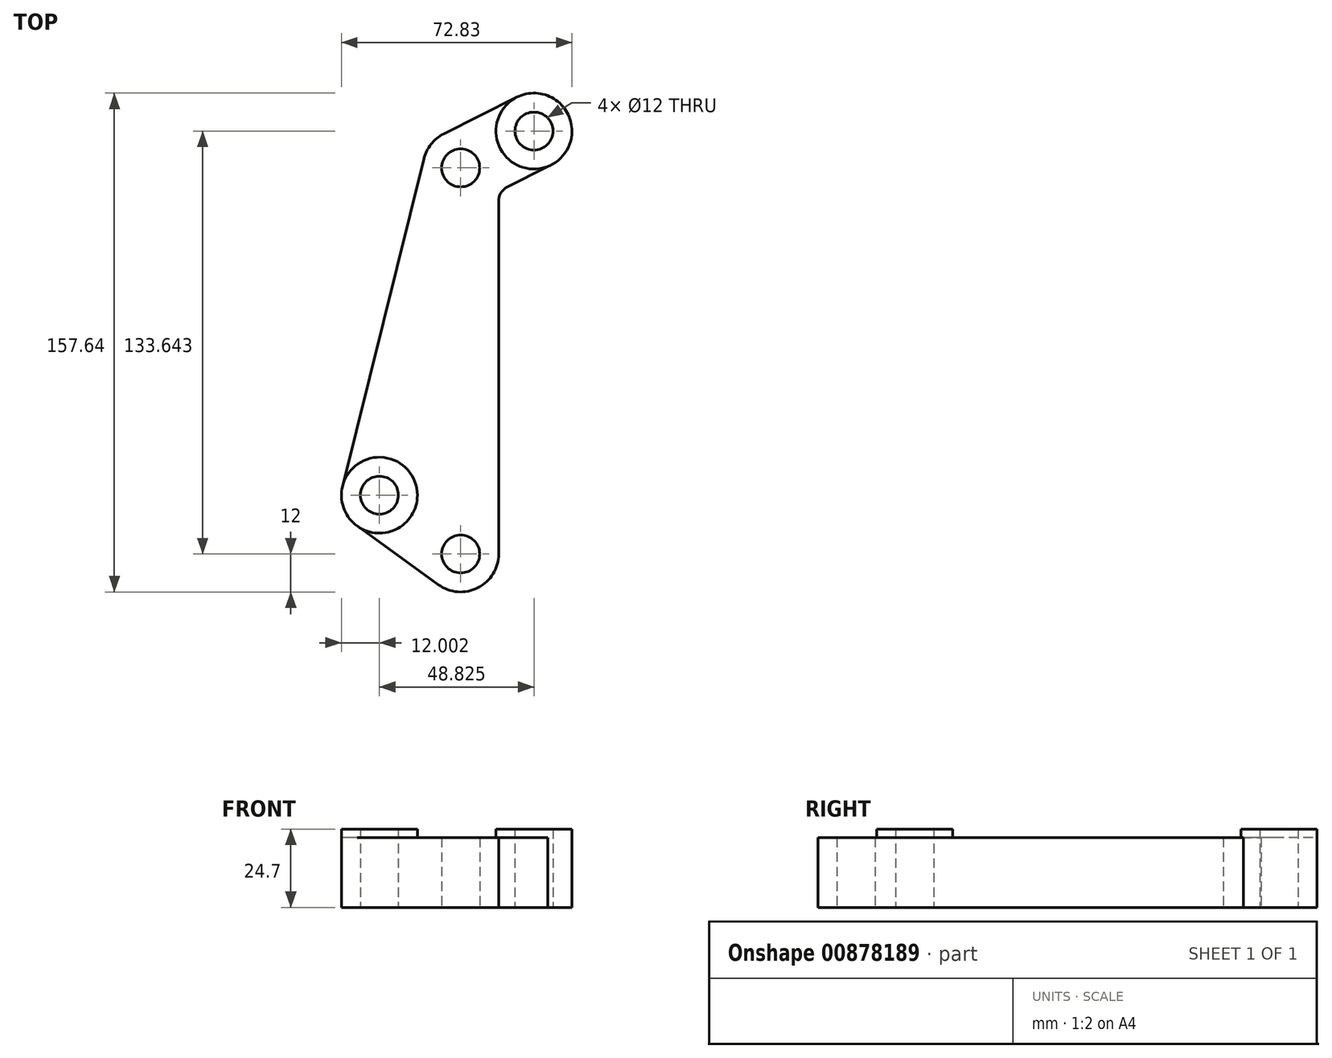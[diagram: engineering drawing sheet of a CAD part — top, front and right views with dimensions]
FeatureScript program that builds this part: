
annotation { "Feature Type Name" : "Feature", "Feature Type Description" : "" }
export const myFeature = defineFeature(function(context is Context, id is Id, definition is map)
    precondition{}
    {
        {
            var Q0;
            Q0=qCreatedBy(makeId("Top.planeOp"),FACE);
            var sketch = newSketch(context, id + "F0", { "sketchPlane" : qUnion([Q0])});
            skCircle(sketch, "E0", {"center": v(0, 0) * mm, "radius": 73.5 * mm, "construction": true});
            skCircle(sketch, "E1", {"center": v(0, 0) * mm, "radius": 70 * mm, "construction": true});
            skCircle(sketch, "E2", {"center": v(-34.34, 61) * mm, "radius": 6 * mm});
            skCircle(sketch, "E3", {"center": v(-34.34, -61) * mm, "radius": 6 * mm});
            skCircle(sketch, "E4", {"center": v(-60.02, -42.43) * mm, "radius": 6 * mm});
            skCircle(sketch, "E5", {"center": v(-11.2, 72.64) * mm, "radius": 6 * mm});
            skLineSegment(sketch, "E6", {"start": v(-11.2, 72.64) * mm, "end": v(-60.02, -42.43) * mm, "construction": true});
            skLineSegment(sketch, "E7", {"start": v(-34.34, 61) * mm, "end": v(-34.34, -61) * mm, "construction": true});
            skCircle(sketch, "E8", {"center": v(-60.02, -42.43) * mm, "radius": 12 * mm});
            skCircle(sketch, "E9", {"center": v(-34.34, -61) * mm, "radius": 12 * mm});
            skCircle(sketch, "E10", {"center": v(-11.2, 72.64) * mm, "radius": 12 * mm});
            skCircle(sketch, "E11", {"center": v(-34.34, 61) * mm, "radius": 12 * mm});
            skLineSegment(sketch, "E12", {"start": v(-34.34, -61) * mm, "end": v(-22.34, -61) * mm});
            skLineSegment(sketch, "E13", {"start": v(-16.59, 83.36) * mm, "end": v(-39.73, 71.72) * mm});
            skLineSegment(sketch, "E14", {"start": v(-45.98, 63.9) * mm, "end": v(-71.66, -39.54) * mm});
            skLineSegment(sketch, "E15", {"start": v(-41.37, -70.72) * mm, "end": v(-67.05, -52.15) * mm});
            skLineSegment(sketch, "E16.trimOffspring", {"start": v(-19.6, 55.01) * mm, "end": v(-6.87, 61.45) * mm});
            skLineSegment(sketch, "E17", {"start": v(-22.34, -61) * mm, "end": v(-22.34, 50.55) * mm});
            skPoint(sketch, "E18.visualSharp", {"position": v(-22.34, 53.62) * mm});
            skArc(sketch, "E18.filletArc", {"start": v(-19.6, 55.01) * mm, "mid": v(-21.6, 53.17) * mm, "end": v(-22.34, 50.55) * mm});
            skPoint(sketch, "E19.start.orphan", {"position": v(-22.34, 61) * mm});
            skSolve(sketch);
        }
        {
            var Q0;
            Q0=makeQuery(id+"F0.imprint","IMPRINT",FACE,{"disambiguationData":[TD([[makeQuery(id+"F0.imprint","IMPRINT",EDGE,{"derivedFrom":sQuery(id+"F0.wireOp",EDGE,"E2")}),-1.0]])]});
            var Q1;
            Q1=makeQuery(id+"F0.imprint","IMPRINT",FACE,{"disambiguationData":[TD([[makeQuery(id+"F0.imprint","IMPRINT",EDGE,{"derivedFrom":sQuery(id+"F0.wireOp",EDGE,"E3")}),-1.0]])]});
            var Q2;
            {var subQ0=sQuery(id+"F0.wireOp",EDGE,"E13");Q2=makeQuery(id+"F0.imprint","IMPRINT",FACE,{"disambiguationData":[TD([[makeQuery(id+"F0.imprint","IMPRINT",EDGE,{"derivedFrom":subQ0}),1.0]])]});}
            extrude(context, id + "F1", {"entities" : qUnion([Q0, Q1, Q2]), "depth" : 22 * mm, "offsetDistance" : 25 * mm});
        }
        {
            var Q0;
            Q0=makeQuery(id+"F0.imprint","IMPRINT",FACE,{"disambiguationData":[TD([[makeQuery(id+"F0.imprint","IMPRINT",EDGE,{"derivedFrom":sQuery(id+"F0.wireOp",EDGE,"E4")}),-1.0]])]});
            var Q1;
            Q1=makeQuery(id+"F0.imprint","IMPRINT",FACE,{"disambiguationData":[TD([[makeQuery(id+"F0.imprint","IMPRINT",EDGE,{"derivedFrom":sQuery(id+"F0.wireOp",EDGE,"E5")}),-1.0]])]});
            extrude(context, id + "F2", {"entities" : qUnion([Q0, Q1]), "operationType" : NewBodyOperationType.ADD, "depth" : 24.7 * mm, "offsetDistance" : 25 * mm});
        }
    });
